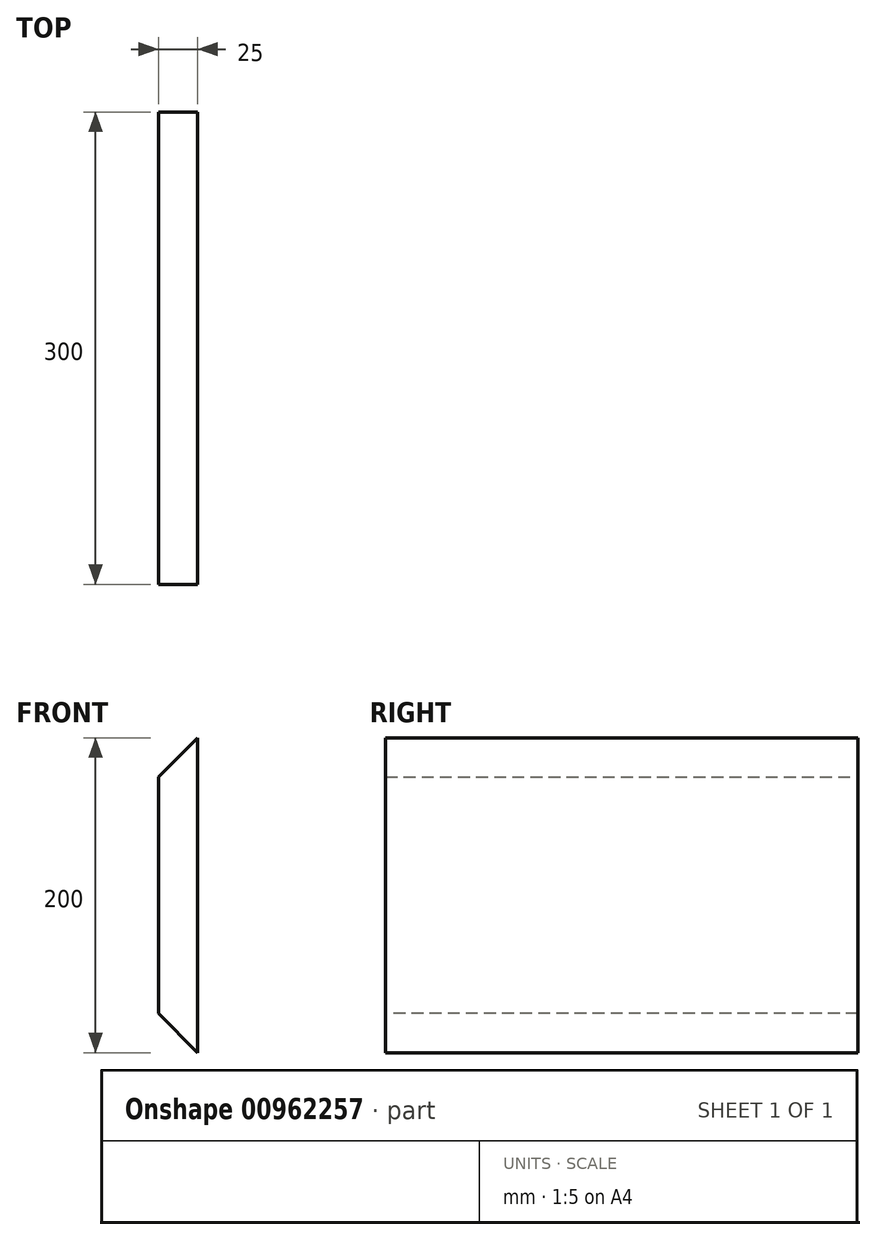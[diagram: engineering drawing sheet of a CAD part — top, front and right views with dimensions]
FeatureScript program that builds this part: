
annotation { "Feature Type Name" : "Feature", "Feature Type Description" : "" }
export const myFeature = defineFeature(function(context is Context, id is Id, definition is map)
    precondition{}
    {
        {
            var Q0;
            Q0=qCreatedBy(makeId("Front.planeOp"),FACE);
            var sketch = newSketch(context, id + "F0", { "sketchPlane" : qUnion([Q0])});
            skLineSegment(sketch, "E0.bottom", {"start": v(0, 0) * mm, "end": v(25, 0) * mm});
            skLineSegment(sketch, "E0.top", {"start": v(0, 200) * mm, "end": v(25, 200) * mm});
            skLineSegment(sketch, "E0.left", {"start": v(0, 0) * mm, "end": v(0, 200) * mm});
            skLineSegment(sketch, "E0.right", {"start": v(25, 0) * mm, "end": v(25, 200) * mm});
            skSolve(sketch);
        }
        {
            var Q0;
            Q0=makeQuery(id+"F0.imprint","IMPRINT",FACE,{"disambiguationData":[TD([[makeQuery(id+"F0.imprint","IMPRINT",EDGE,{"derivedFrom":sQuery(id+"F0.wireOp",EDGE,"E0.bottom")}),1.0]])]});
            extrude(context, id + "F1", {"entities" : qUnion([Q0]), "depth" : 300 * mm, "offsetDistance" : 25 * mm});
        }
        {
            var Q0;
            Q0=makeQuery(id+"F1.opExtrude","SWEPT_EDGE",EDGE,{"disambiguationData":[OSD([sQuery(id+"F0.wireOp",EDGE,"E0.top"),sQuery(id+"F0.wireOp",EDGE,"E0.left")])]});
            chamfer(context, id + "F2", {"entities" : qUnion([Q0]), "width" : 25 * mm, "tangentPropagation" : true});
        }
        {
            var Q0;
            Q0=makeQuery(id+"F1.opExtrude","SWEPT_EDGE",EDGE,{"disambiguationData":[OSD([sQuery(id+"F0.wireOp",EDGE,"E0.bottom"),sQuery(id+"F0.wireOp",EDGE,"E0.left")])]});
            chamfer(context, id + "F3", {"entities" : qUnion([Q0]), "width" : 25 * mm, "tangentPropagation" : true});
        }
    });
